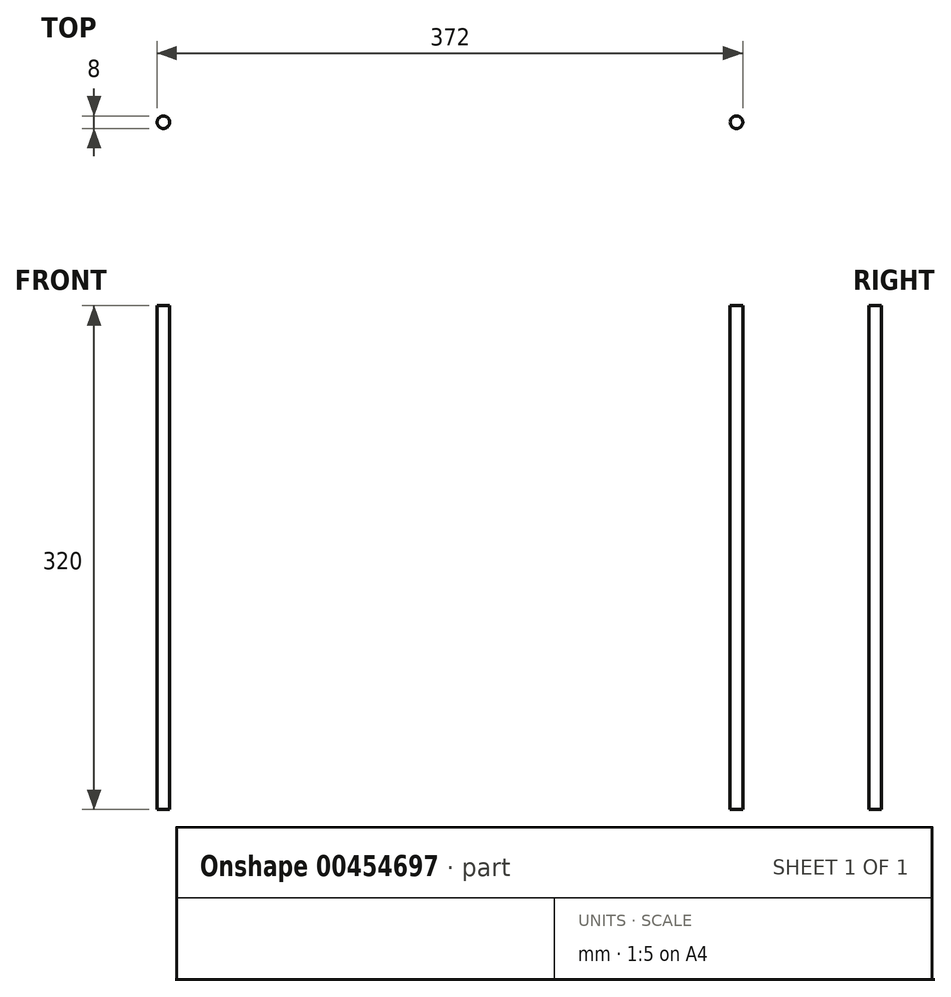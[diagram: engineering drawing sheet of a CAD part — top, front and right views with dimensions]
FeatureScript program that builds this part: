
annotation { "Feature Type Name" : "Feature", "Feature Type Description" : "" }
export const myFeature = defineFeature(function(context is Context, id is Id, definition is map)
    precondition{}
    {
        {
            var Q0;
            Q0=qCreatedBy(makeId("Top.planeOp"),FACE);
            var sketch = newSketch(context, id + "F0", { "sketchPlane" : qUnion([Q0])});
            skCircle(sketch, "E0", {"center": v(0, 0) * mm, "radius": 4 * mm});
            skCircle(sketch, "E1", {"center": v(-364, 0) * mm, "radius": 4 * mm});
            skSolve(sketch);
        }
        {
            var Q0;
            Q0=qSketchRegion(id+"F0",true);
            extrude(context, id + "F1", {"entities" : qUnion([Q0]), "oppositeDirection" : true, "depth" : 320 * mm});
        }
    });
